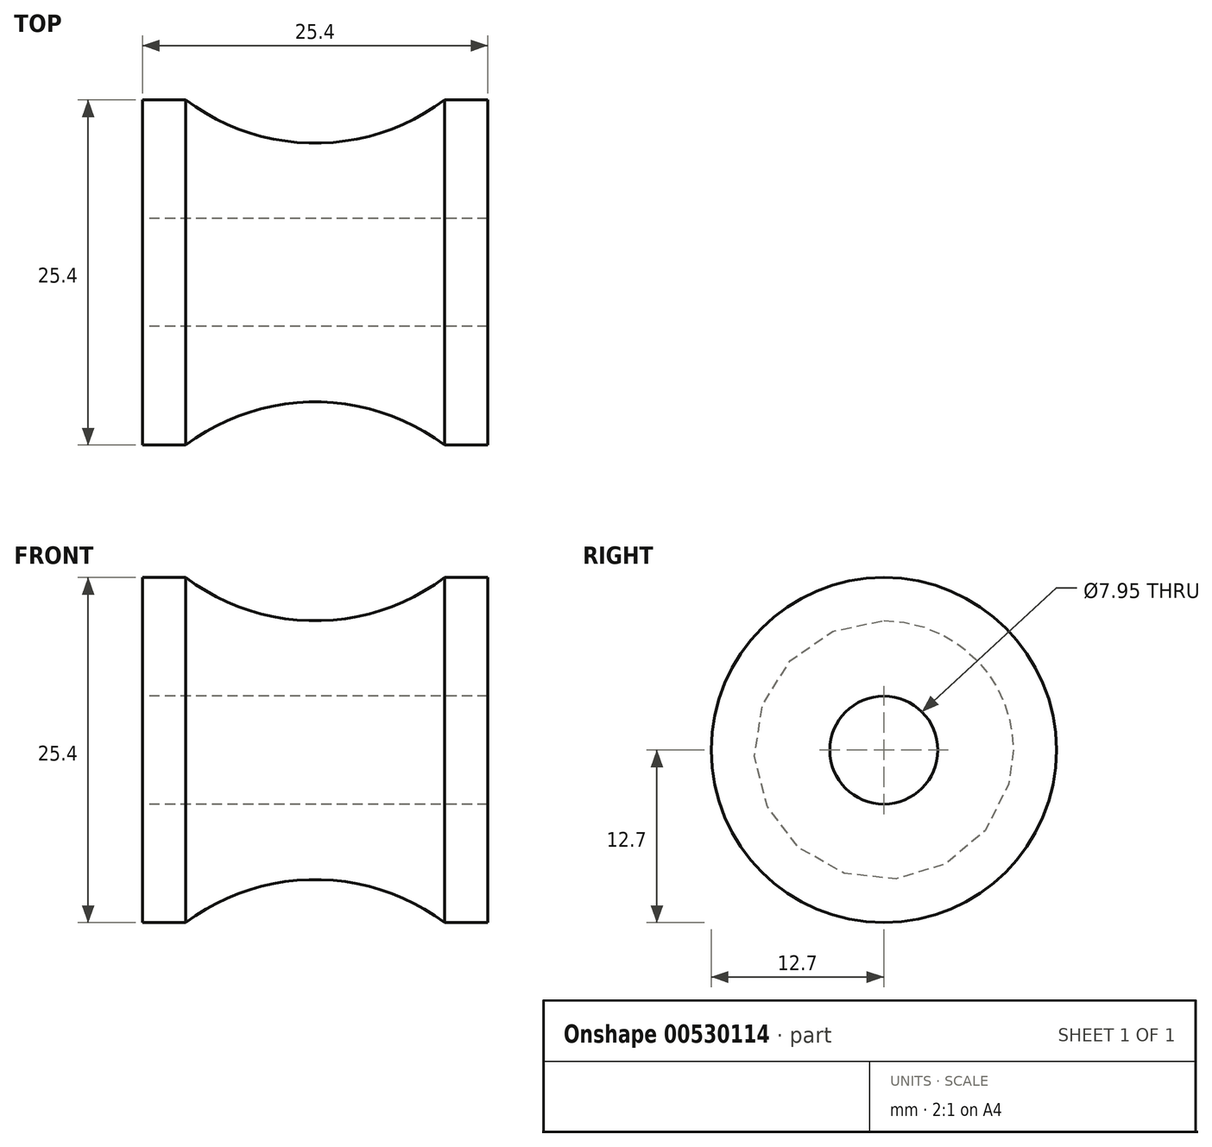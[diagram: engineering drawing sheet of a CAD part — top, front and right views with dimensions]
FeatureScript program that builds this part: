
annotation { "Feature Type Name" : "Feature", "Feature Type Description" : "" }
export const myFeature = defineFeature(function(context is Context, id is Id, definition is map)
    precondition{}
    {
        {
            var Q0;
            Q0=qCreatedBy(makeId("Front.planeOp"),FACE);
            var sketch = newSketch(context, id + "F0", { "sketchPlane" : qUnion([Q0])});
            skLineSegment(sketch, "E0", {"start": v(-12.7, 3.98) * mm, "end": v(-12.7, 12.7) * mm});
            skLineSegment(sketch, "E1", {"start": v(-12.7, 12.7) * mm, "end": v(-9.52, 12.7) * mm});
            skLineSegment(sketch, "E2", {"start": v(12.7, 3.98) * mm, "end": v(12.7, 12.7) * mm});
            skLineSegment(sketch, "E3", {"start": v(12.7, 12.7) * mm, "end": v(9.53, 12.7) * mm});
            skArc(sketch, "E4", {"start": v(-9.53, 12.7) * mm, "mid": v(0, 9.52) * mm, "end": v(9.53, 12.7) * mm});
            skLineSegment(sketch, "E5", {"start": v(0, 21.26) * mm, "end": v(0, -14.72) * mm, "construction": true});
            skLineSegment(sketch, "E6", {"start": v(-21.92, 0) * mm, "end": v(26.46, 0) * mm, "construction": true});
            skLineSegment(sketch, "E7", {"start": v(-12.7, 3.98) * mm, "end": v(12.7, 3.98) * mm});
            skSolve(sketch);
        }
        {
            var Q0;
            Q0=makeQuery(id+"F0.imprint","IMPRINT",FACE,{"disambiguationData":[TD([[makeQuery(id+"F0.imprint","IMPRINT",EDGE,{"derivedFrom":sQuery(id+"F0.wireOp",EDGE,"TZ9rcT85-0ArW-pqXl-cVuh-IrIEBctlaAR6")}),1.0]])]});
            var Q1;
            Q1 = qSketchRegion(id + "F0", true);
            var Q2;
            Q2=sQuery(id+"F0.wireOp",EDGE,"E6");
            revolve(context, id + "F1", {"entities" : qUnion([Q0, Q1]), "axis" : qUnion([Q2]), "revolveType" : RevolveType.FULL});
        }
    });
